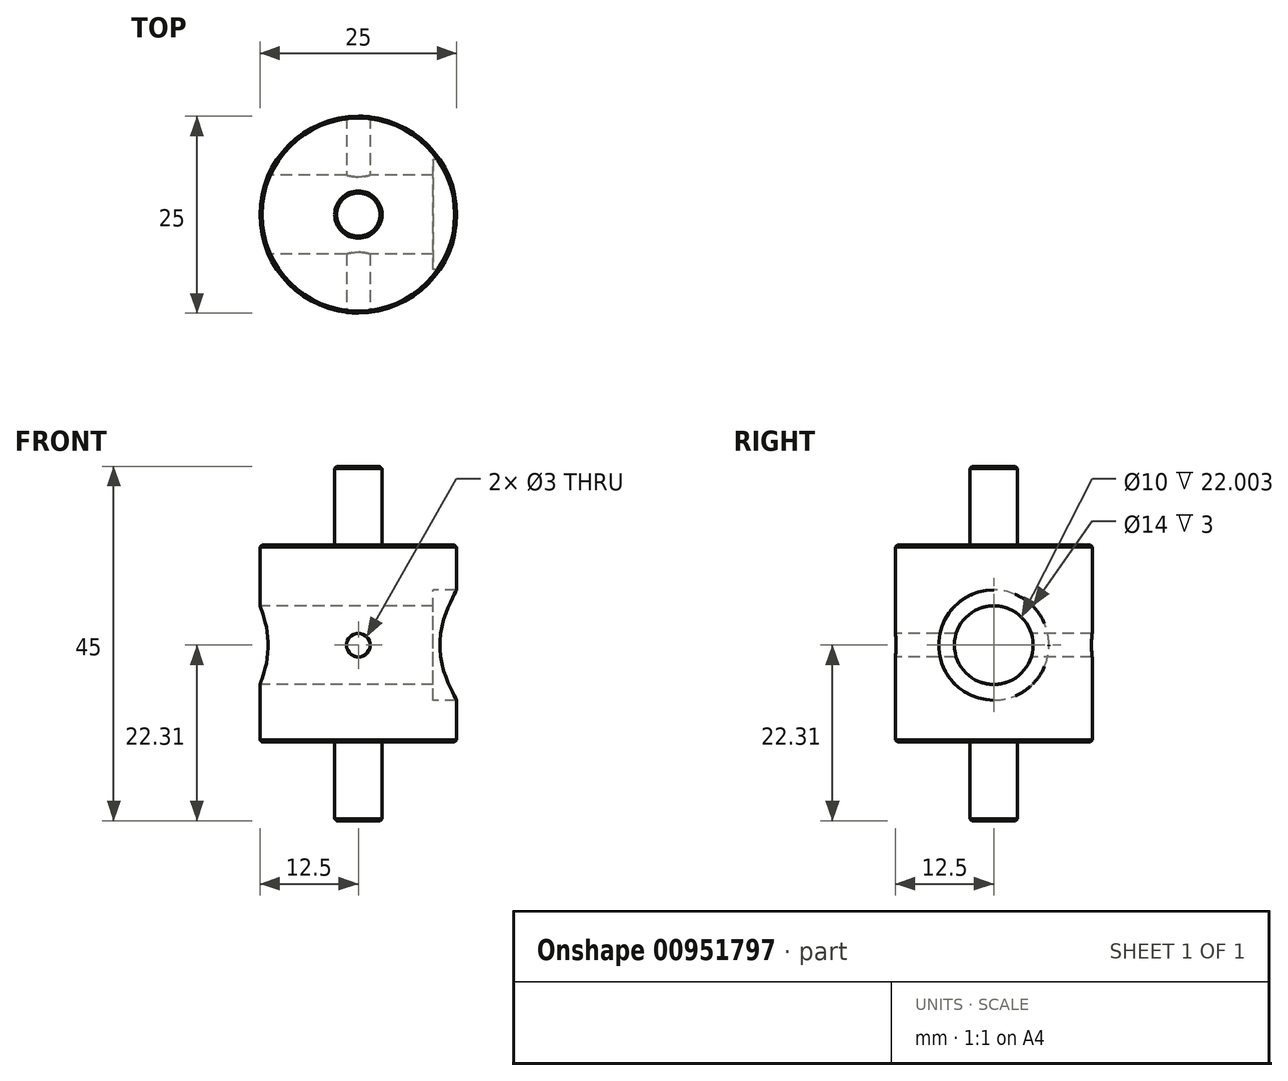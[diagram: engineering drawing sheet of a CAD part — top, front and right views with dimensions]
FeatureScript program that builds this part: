
annotation { "Feature Type Name" : "Feature", "Feature Type Description" : "" }
export const myFeature = defineFeature(function(context is Context, id is Id, definition is map)
    precondition{}
    {
        {
            var Q0;
            Q0=qCreatedBy(makeId("Front.planeOp"),FACE);
            var sketch = newSketch(context, id + "F0", { "sketchPlane" : qUnion([Q0])});
            skLineSegment(sketch, "E0", {"start": v(0, 22.69) * mm, "end": v(-3, 22.69) * mm});
            skLineSegment(sketch, "E1", {"start": v(-3, 22.69) * mm, "end": v(-3, 12.69) * mm});
            skLineSegment(sketch, "E2", {"start": v(-3, 12.69) * mm, "end": v(-12.5, 12.69) * mm});
            skLineSegment(sketch, "E3", {"start": v(-12.5, 12.69) * mm, "end": v(-12.5, -12.31) * mm});
            skLineSegment(sketch, "E4", {"start": v(-12.5, -12.31) * mm, "end": v(-3, -12.31) * mm});
            skLineSegment(sketch, "E5", {"start": v(-3, -12.31) * mm, "end": v(-3, -22.31) * mm});
            skLineSegment(sketch, "E6", {"start": v(-3, -22.31) * mm, "end": v(0, -22.31) * mm});
            skLineSegment(sketch, "E7", {"start": v(0, 22.69) * mm, "end": v(0, -22.31) * mm});
            skSolve(sketch);
        }
        {
            var Q0;
            Q0=makeQuery(id+"F0.imprint","IMPRINT",FACE,{"disambiguationData":[TD([[makeQuery(id+"F0.imprint","IMPRINT",EDGE,{"derivedFrom":sQuery(id+"F0.wireOp",EDGE,"E0")}),1.0]])]});
            var Q1;
            Q1=sQuery(id+"F0.wireOp",EDGE,"E7");
            revolve(context, id + "F1", {"surfaceOperationType" : NewSurfaceOperationType.NEW, "entities" : qUnion([Q0]), "axis" : qUnion([Q1]), "revolveType" : RevolveType.FULL});
        }
        {
            var Q0;
            Q0=makeQuery(id+"F1.opRevolve","SWEPT_EDGE",EDGE,{"disambiguationData":[OSD([sQuery(id+"F0.wireOp",EDGE,"E0"),sQuery(id+"F0.wireOp",EDGE,"E1")])]});
            var Q1;
            Q1=makeQuery(id+"F1.opRevolve","SWEPT_EDGE",EDGE,{"disambiguationData":[OSD([sQuery(id+"F0.wireOp",EDGE,"E5"),sQuery(id+"F0.wireOp",EDGE,"E6")])]});
            var Q2;
            Q2=makeQuery(id+"F1.opRevolve","SWEPT_EDGE",EDGE,{"disambiguationData":[OSD([sQuery(id+"F0.wireOp",EDGE,"E2"),sQuery(id+"F0.wireOp",EDGE,"E3")])]});
            var Q3;
            Q3=makeQuery(id+"F1.opRevolve","SWEPT_EDGE",EDGE,{"disambiguationData":[OSD([sQuery(id+"F0.wireOp",EDGE,"E3"),sQuery(id+"F0.wireOp",EDGE,"E4")])]});
            chamfer(context, id + "F2", {"entities" : qUnion([Q0, Q1, Q2, Q3]), "width" : 0.25 * mm, "tangentPropagation" : true});
        }
        {
            var Q0;
            Q0=qCreatedBy(makeId("Front.planeOp"),FACE);
            var sketch = newSketch(context, id + "F3", { "sketchPlane" : qUnion([Q0])});
            skCircle(sketch, "E8", {"center": v(0, 0) * mm, "radius": 1.5 * mm});
            skSolve(sketch);
        }
        {
            var Q0;
            Q0=qCreatedBy(makeId("Right.planeOp"),FACE);
            var sketch = newSketch(context, id + "F4", { "sketchPlane" : qUnion([Q0])});
            skCircle(sketch, "E9", {"center": v(0, 0) * mm, "radius": 5 * mm});
            skSolve(sketch);
        }
        {
            var Q0;
            Q0 = qSketchRegion(id + "F3", true);
            extrude(context, id + "F5", {"entities" : qUnion([Q0]), "operationType" : NewBodyOperationType.REMOVE, "oppositeDirection" : true, "depth" : 25 * mm, "offsetDistance" : 25 * mm, "symmetric" : true});
        }
        {
            var Q0;
            Q0 = qSketchRegion(id + "F4", true);
            extrude(context, id + "F6", {"entities" : qUnion([Q0]), "operationType" : NewBodyOperationType.REMOVE, "depth" : 25 * mm, "offsetDistance" : 25 * mm, "symmetric" : true});
        }
        {
            var Q0;
            Q0=qCreatedBy(makeId("Right.planeOp"),FACE);
            var sketch = newSketch(context, id + "F7", { "sketchPlane" : qUnion([Q0])});
            skCircle(sketch, "E10", {"center": v(0, 0) * mm, "radius": 7 * mm});
            skSolve(sketch);
        }
        {
            var Q0;
            Q0 = qSketchRegion(id + "F7", true);
            extrude(context, id + "F8", {"entities" : qUnion([Q0]), "operationType" : NewBodyOperationType.REMOVE, "depth" : 14 * mm, "offsetDistance" : 25 * mm, "hasSecondDirection" : true, "secondDirectionOppositeDirection" : false, "secondDirectionDepth" : 9.5 * mm});
        }
    });
